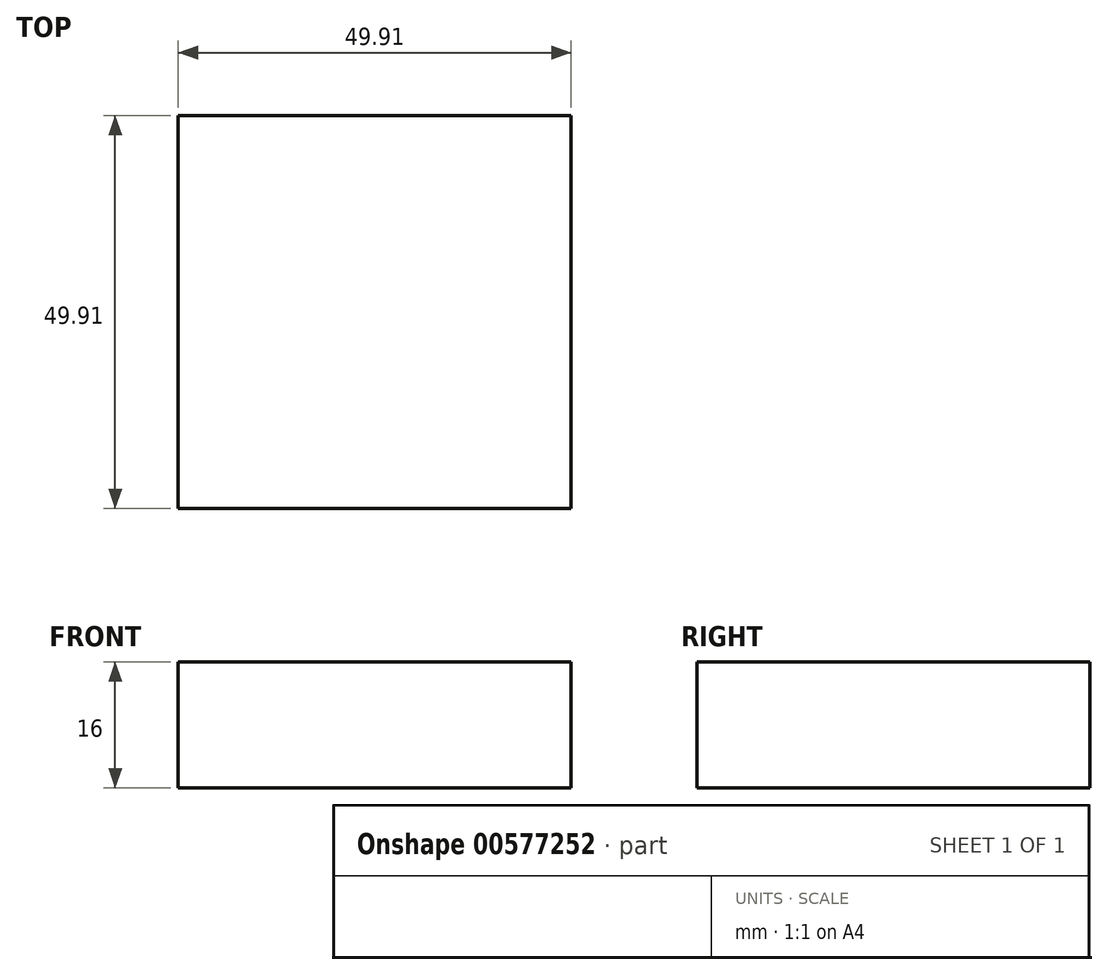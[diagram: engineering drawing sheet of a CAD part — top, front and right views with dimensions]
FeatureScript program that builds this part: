
annotation { "Feature Type Name" : "Feature", "Feature Type Description" : "" }
export const myFeature = defineFeature(function(context is Context, id is Id, definition is map)
    precondition{}
    {
        {
            var Q0;
            Q0=qCreatedBy(makeId("Top.planeOp"),FACE);
            var sketch = newSketch(context, id + "F0", { "sketchPlane" : qUnion([Q0])});
            skLineSegment(sketch, "E0.bottom", {"start": v(0, 0) * mm, "end": v(-49.91, 0) * mm});
            skLineSegment(sketch, "E0.top", {"start": v(0, 49.91) * mm, "end": v(-49.91, 49.91) * mm});
            skLineSegment(sketch, "E0.left", {"start": v(0, 0) * mm, "end": v(0, 49.91) * mm});
            skLineSegment(sketch, "E0.right", {"start": v(-49.91, 0) * mm, "end": v(-49.91, 49.91) * mm});
            skPoint(sketch, "E0.middle", {"position": v(-24.96, 24.96) * mm});
            skSolve(sketch);
        }
        {
            var Q0;
            Q0 = qSketchRegion(id + "F0", true);
            extrude(context, id + "F1", {"entities" : qUnion([Q0]), "depth" : 16 * mm, "offsetDistance" : 25.4 * mm});
        }
    });
